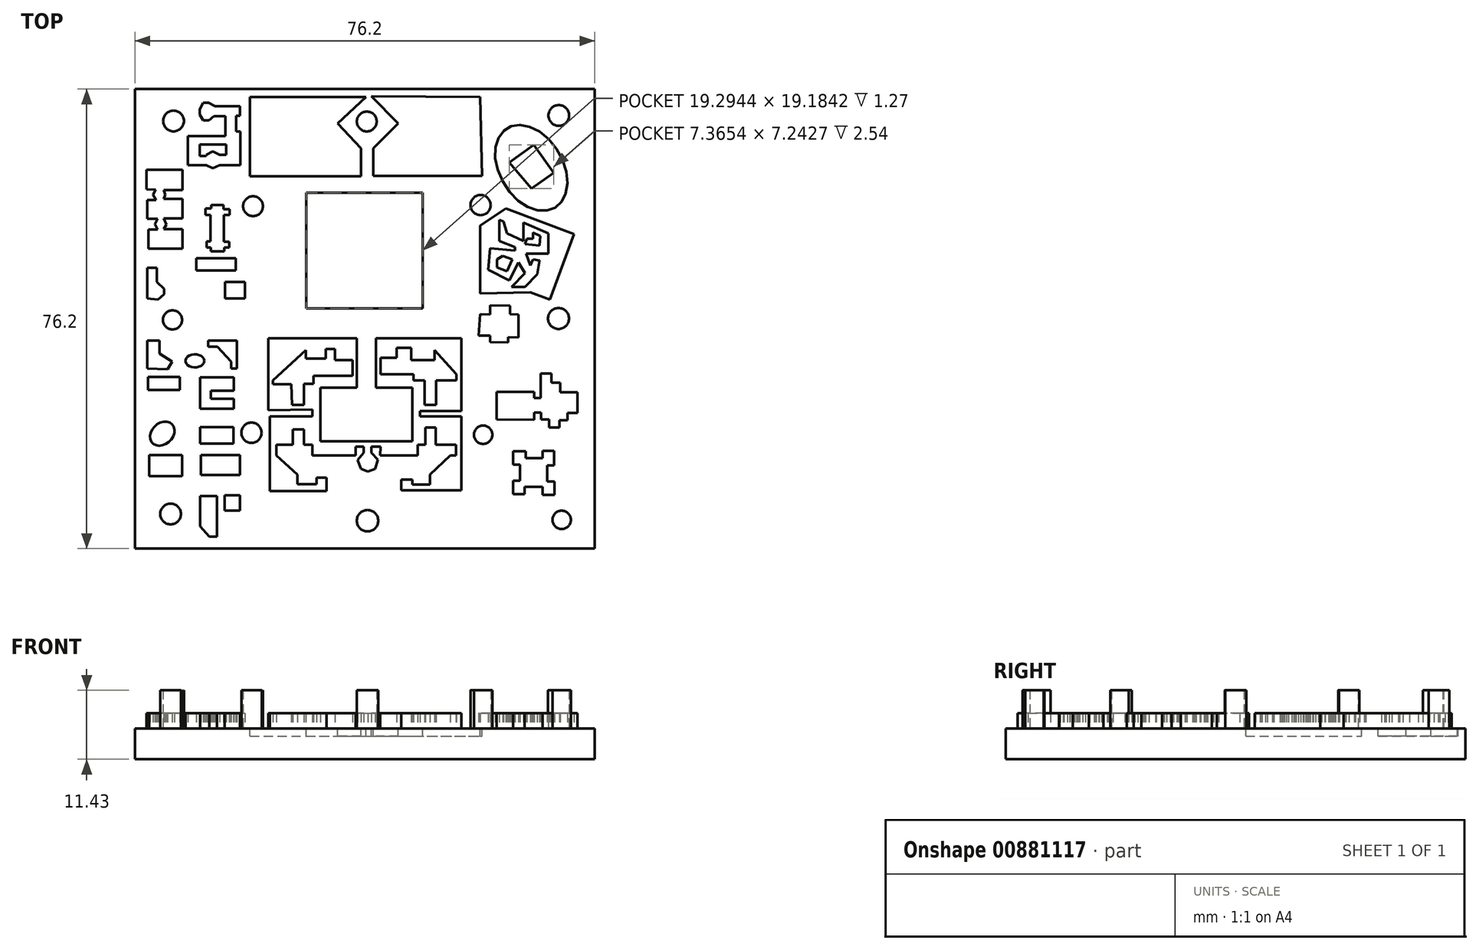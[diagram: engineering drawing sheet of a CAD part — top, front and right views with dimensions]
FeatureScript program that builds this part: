
annotation { "Feature Type Name" : "Feature", "Feature Type Description" : "" }
export const myFeature = defineFeature(function(context is Context, id is Id, definition is map)
    precondition{}
    {
        {
            var Q0;
            Q0=qCreatedBy(makeId("Top.planeOp"),FACE);
            var sketch = newSketch(context, id + "F0", { "sketchPlane" : qUnion([Q0])});
            skSolve(sketch);
        }
        {
            var Q0;
            Q0=qCreatedBy(makeId("Top.planeOp"),FACE);
            var sketch = newSketch(context, id + "F1", { "sketchPlane" : qUnion([Q0])});
            skLineSegment(sketch, "E0.bottom", {"start": v(-39.17, -36.08) * mm, "end": v(37.03, -36.08) * mm});
            skLineSegment(sketch, "E0.top", {"start": v(-39.17, 40.12) * mm, "end": v(37.03, 40.12) * mm});
            skLineSegment(sketch, "E0.left", {"start": v(-39.17, -36.08) * mm, "end": v(-39.17, 40.12) * mm});
            skLineSegment(sketch, "E0.right", {"start": v(37.03, -36.08) * mm, "end": v(37.03, 40.12) * mm});
            skSolve(sketch);
        }
        {
            var Q0;
            Q0 = qSketchRegion(id + "F1", true);
            extrude(context, id + "F2", {"entities" : qUnion([Q0]), "oppositeDirection" : true, "depth" : 5.08 * mm, "offsetDistance" : 25.4 * mm});
        }
        {
            var Q0;
            Q0=makeQuery(id+"F2.opExtrude","CAP_FACE",FACE,{"disambiguationData":[OSD([sQuery(id+"F1.wireOp",EDGE,"E0.bottom"),sQuery(id+"F1.wireOp",EDGE,"E0.top"),sQuery(id+"F1.wireOp",EDGE,"E0.left"),sQuery(id+"F1.wireOp",EDGE,"E0.right")])],"isStart":true});
            var sketch = newSketch(context, id + "F3", { "sketchPlane" : qUnion([Q0])});
            skCircle(sketch, "E1", {"center": v(-0.74, 34.74) * mm, "radius": 1.65 * mm});
            skCircle(sketch, "E2", {"center": v(-19.6, 20.7) * mm, "radius": 1.65 * mm});
            skCircle(sketch, "E3", {"center": v(-32.95, 1.84) * mm, "radius": 1.58 * mm});
            skCircle(sketch, "E4", {"center": v(-32.78, 34.83) * mm, "radius": 1.72 * mm});
            skCircle(sketch, "E5", {"center": v(18.13, 20.88) * mm, "radius": 1.67 * mm});
            skCircle(sketch, "E6", {"center": v(31.1, 35.74) * mm, "radius": 1.72 * mm});
            skCircle(sketch, "E7", {"center": v(31.04, 2.08) * mm, "radius": 1.74 * mm});
            skCircle(sketch, "E8", {"center": v(18.54, -17.2) * mm, "radius": 1.52 * mm});
            skCircle(sketch, "E9", {"center": v(-0.61, -31.45) * mm, "radius": 1.78 * mm});
            skCircle(sketch, "E10", {"center": v(-19.85, -16.87) * mm, "radius": 1.68 * mm});
            skCircle(sketch, "E11", {"center": v(-33.26, -30.34) * mm, "radius": 1.72 * mm});
            skCircle(sketch, "E12", {"center": v(31.56, -31.31) * mm, "radius": 1.52 * mm});
            skSolve(sketch);
        }
        {
            var Q0;
            Q0 = qSketchRegion(id + "F3", true);
            extrude(context, id + "F4", {"entities" : qUnion([Q0]), "operationType" : NewBodyOperationType.ADD, "depth" : 6.35 * mm, "offsetDistance" : 25.4 * mm});
        }
        {
            var Q0;
            Q0=makeQuery(id+"F2.opExtrude","CAP_FACE",FACE,{"disambiguationData":[OSD([sQuery(id+"F1.wireOp",EDGE,"E0.bottom"),sQuery(id+"F1.wireOp",EDGE,"E0.top"),sQuery(id+"F1.wireOp",EDGE,"E0.left"),sQuery(id+"F1.wireOp",EDGE,"E0.right")])],"isStart":true});
            var sketch = newSketch(context, id + "F5", { "sketchPlane" : qUnion([Q0])});
            skLineSegment(sketch, "E13.bottom", {"start": v(-10.75, 3.73) * mm, "end": v(8.55, 3.73) * mm});
            skLineSegment(sketch, "E13.top", {"start": v(-10.75, 22.91) * mm, "end": v(8.55, 22.91) * mm});
            skLineSegment(sketch, "E13.left", {"start": v(-10.75, 3.73) * mm, "end": v(-10.75, 22.91) * mm});
            skLineSegment(sketch, "E13.right", {"start": v(8.55, 3.73) * mm, "end": v(8.55, 22.91) * mm});
            skLineSegment(sketch, "E14", {"start": v(-20.12, 25.67) * mm, "end": v(-1.7, 25.67) * mm});
            skLineSegment(sketch, "E15", {"start": v(-1.7, 25.67) * mm, "end": v(-1.7, 30.3) * mm});
            skLineSegment(sketch, "E16", {"start": v(-1.7, 30.3) * mm, "end": v(-5.57, 34.4) * mm});
            skLineSegment(sketch, "E17", {"start": v(4.49, 34.4) * mm, "end": v(0.33, 30.3) * mm});
            skLineSegment(sketch, "E18", {"start": v(0.33, 30.3) * mm, "end": v(0.33, 25.7) * mm});
            skLineSegment(sketch, "E19", {"start": v(0.33, 25.7) * mm, "end": v(18.38, 25.7) * mm});
            skLineSegment(sketch, "E20", {"start": v(-20.12, 40.12) * mm, "end": v(-0.63, 40.12) * mm});
            skLineSegment(sketch, "E21", {"start": v(18.38, 40.12) * mm, "end": v(-0.63, 40.12) * mm});
            skLineSegment(sketch, "E22", {"start": v(-5.57, 34.4) * mm, "end": v(-0.88, 38.83) * mm});
            skLineSegment(sketch, "E23", {"start": v(4.49, 34.4) * mm, "end": v(0, 38.95) * mm});
            skLineSegment(sketch, "E24", {"start": v(-20.12, 25.67) * mm, "end": v(-20.12, 38.83) * mm});
            skLineSegment(sketch, "E25", {"start": v(18.04, 38.83) * mm, "end": v(18.38, 25.7) * mm});
            skLineSegment(sketch, "E26", {"start": v(-20.12, 38.83) * mm, "end": v(-0.88, 38.83) * mm});
            skLineSegment(sketch, "E27", {"start": v(0, 38.95) * mm, "end": v(18.04, 38.83) * mm});
            skSolve(sketch);
        }
        {
            var Q0;
            Q0 = qSketchRegion(id + "F5", true);
            extrude(context, id + "F6", {"entities" : qUnion([Q0]), "operationType" : NewBodyOperationType.REMOVE, "oppositeDirection" : true, "depth" : 1.27 * mm, "offsetDistance" : 25.4 * mm});
        }
        {
            var Q0;
            Q0=makeQuery(id+"F1.imprint","IMPRINT",FACE,{"disambiguationData":[TD([[makeQuery(id+"F1.imprint","IMPRINT",EDGE,{"derivedFrom":sQuery(id+"F1.wireOp",EDGE,"E0.bottom")}),1.0]])]});
            var sketch = newSketch(context, id + "F7", { "sketchPlane" : qUnion([Q0])});
            skLineSegment(sketch, "E28", {"start": v(-17.08, -13.15) * mm, "end": v(-17.08, -1.2) * mm});
            skLineSegment(sketch, "E29", {"start": v(-17.08, -1.2) * mm, "end": v(-2.39, -1.2) * mm});
            skLineSegment(sketch, "E30", {"start": v(-2.39, -1.2) * mm, "end": v(-2.39, -9.4) * mm});
            skLineSegment(sketch, "E31", {"start": v(-2.39, -9.4) * mm, "end": v(-8.41, -9.4) * mm});
            skLineSegment(sketch, "E32", {"start": v(-8.41, -9.4) * mm, "end": v(-8.41, -18.26) * mm});
            skLineSegment(sketch, "E33", {"start": v(-8.41, -18.26) * mm, "end": v(6.83, -18.26) * mm});
            skLineSegment(sketch, "E34", {"start": v(6.83, -18.26) * mm, "end": v(6.83, -9.4) * mm});
            skLineSegment(sketch, "E35", {"start": v(6.83, -9.4) * mm, "end": v(0.8, -9.4) * mm});
            skLineSegment(sketch, "E36", {"start": v(0.8, -9.4) * mm, "end": v(0.8, -1.2) * mm});
            skLineSegment(sketch, "E37", {"start": v(0.8, -1.2) * mm, "end": v(14.95, -1.2) * mm});
            skLineSegment(sketch, "E38", {"start": v(14.95, -1.2) * mm, "end": v(14.95, -13.24) * mm});
            skLineSegment(sketch, "E39", {"start": v(14.95, -13.24) * mm, "end": v(8.1, -13.24) * mm});
            skLineSegment(sketch, "E40", {"start": v(8.1, -13.24) * mm, "end": v(8.1, -14.15) * mm});
            skLineSegment(sketch, "E41", {"start": v(8.1, -14.15) * mm, "end": v(14.95, -14.15) * mm});
            skLineSegment(sketch, "E42", {"start": v(14.95, -14.15) * mm, "end": v(14.95, -26.38) * mm});
            skLineSegment(sketch, "E43", {"start": v(14.95, -26.38) * mm, "end": v(5, -26.38) * mm});
            skLineSegment(sketch, "E44", {"start": v(5, -26.38) * mm, "end": v(5, -24.65) * mm});
            skLineSegment(sketch, "E45", {"start": v(5, -24.65) * mm, "end": v(6.83, -24.65) * mm});
            skLineSegment(sketch, "E46", {"start": v(6.83, -24.65) * mm, "end": v(6.83, -25.47) * mm});
            skLineSegment(sketch, "E47", {"start": v(6.83, -25.47) * mm, "end": v(9.75, -25.47) * mm});
            skLineSegment(sketch, "E48", {"start": v(9.75, -25.47) * mm, "end": v(9.75, -23.83) * mm});
            skLineSegment(sketch, "E49", {"start": v(9.75, -23.83) * mm, "end": v(13.12, -20.63) * mm});
            skLineSegment(sketch, "E50", {"start": v(13.12, -20.63) * mm, "end": v(14.04, -20.63) * mm});
            skLineSegment(sketch, "E51", {"start": v(14.04, -20.63) * mm, "end": v(14.04, -18.85) * mm});
            skLineSegment(sketch, "E52", {"start": v(14.04, -18.85) * mm, "end": v(10.67, -18.85) * mm});
            skLineSegment(sketch, "E53", {"start": v(10.67, -18.85) * mm, "end": v(10.67, -15.97) * mm});
            skLineSegment(sketch, "E54", {"start": v(10.67, -15.97) * mm, "end": v(8.98, -15.97) * mm});
            skLineSegment(sketch, "E55", {"start": v(8.98, -15.97) * mm, "end": v(8.98, -18.85) * mm});
            skLineSegment(sketch, "E56", {"start": v(8.98, -18.85) * mm, "end": v(7.68, -18.85) * mm});
            skLineSegment(sketch, "E57", {"start": v(7.68, -18.85) * mm, "end": v(7.68, -20.63) * mm});
            skLineSegment(sketch, "E58", {"start": v(7.68, -20.63) * mm, "end": v(1.5, -20.63) * mm});
            skLineSegment(sketch, "E59", {"start": v(-1.7, -22.86) * mm, "end": v(-2.25, -21.4) * mm});
            skLineSegment(sketch, "E60", {"start": v(-9.79, -20.64) * mm, "end": v(-9.79, -18.85) * mm});
            skLineSegment(sketch, "E61", {"start": v(-9.79, -18.85) * mm, "end": v(-11.15, -18.85) * mm});
            skLineSegment(sketch, "E62", {"start": v(-11.15, -18.85) * mm, "end": v(-11.15, -16.3) * mm});
            skLineSegment(sketch, "E63", {"start": v(-11.15, -16.3) * mm, "end": v(-13, -16.3) * mm});
            skLineSegment(sketch, "E64", {"start": v(-13, -16.3) * mm, "end": v(-13, -18.85) * mm});
            skLineSegment(sketch, "E65", {"start": v(-13, -18.85) * mm, "end": v(-15.76, -18.85) * mm});
            skLineSegment(sketch, "E66", {"start": v(-15.76, -18.85) * mm, "end": v(-15.76, -20.64) * mm});
            skLineSegment(sketch, "E67", {"start": v(-15.76, -20.64) * mm, "end": v(-12.23, -23.84) * mm});
            skLineSegment(sketch, "E68", {"start": v(-12.23, -23.84) * mm, "end": v(-12.23, -25.41) * mm});
            skLineSegment(sketch, "E69", {"start": v(-12.23, -25.41) * mm, "end": v(-9.08, -25.41) * mm});
            skLineSegment(sketch, "E70", {"start": v(-9.08, -25.41) * mm, "end": v(-9.08, -24.33) * mm});
            skLineSegment(sketch, "E71", {"start": v(-9.08, -24.33) * mm, "end": v(-7.4, -24.33) * mm});
            skLineSegment(sketch, "E72", {"start": v(-7.4, -24.33) * mm, "end": v(-7.4, -26.55) * mm});
            skLineSegment(sketch, "E73", {"start": v(-7.4, -26.55) * mm, "end": v(-16.79, -26.55) * mm});
            skLineSegment(sketch, "E74", {"start": v(-16.79, -26.55) * mm, "end": v(-16.79, -14.18) * mm});
            skLineSegment(sketch, "E75", {"start": v(-16.79, -14.18) * mm, "end": v(-9.79, -14.18) * mm});
            skLineSegment(sketch, "E76", {"start": v(-9.79, -14.18) * mm, "end": v(-9.79, -13.04) * mm});
            skLineSegment(sketch, "E77", {"start": v(-9.79, -13.04) * mm, "end": v(-17.08, -13.15) * mm});
            skLineSegment(sketch, "E78", {"start": v(-13.15, -12.28) * mm, "end": v(-11.15, -12.28) * mm});
            skLineSegment(sketch, "E79", {"start": v(-11.15, -12.28) * mm, "end": v(-11.15, -8.75) * mm});
            skLineSegment(sketch, "E80", {"start": v(-11.15, -8.75) * mm, "end": v(-9.57, -8.75) * mm});
            skLineSegment(sketch, "E81", {"start": v(-9.57, -8.75) * mm, "end": v(-9.57, -7.4) * mm});
            skLineSegment(sketch, "E82", {"start": v(-9.57, -7.4) * mm, "end": v(-3.12, -7.4) * mm});
            skLineSegment(sketch, "E83", {"start": v(-3.12, -7.4) * mm, "end": v(-3.12, -4.8) * mm});
            skLineSegment(sketch, "E84", {"start": v(-3.12, -4.8) * mm, "end": v(-6.05, -4.8) * mm});
            skLineSegment(sketch, "E85", {"start": v(-6.05, -4.8) * mm, "end": v(-6.05, -2.95) * mm});
            skLineSegment(sketch, "E86", {"start": v(-6.05, -2.95) * mm, "end": v(-7.57, -2.95) * mm});
            skLineSegment(sketch, "E87", {"start": v(-7.57, -2.95) * mm, "end": v(-7.57, -4.58) * mm});
            skLineSegment(sketch, "E88", {"start": v(-7.57, -4.58) * mm, "end": v(-10.82, -4.58) * mm});
            skLineSegment(sketch, "E89", {"start": v(-10.82, -4.58) * mm, "end": v(-10.82, -3.16) * mm});
            skLineSegment(sketch, "E90", {"start": v(-10.82, -3.16) * mm, "end": v(-16.3, -8.21) * mm});
            skLineSegment(sketch, "E91", {"start": v(-16.3, -8.21) * mm, "end": v(-16.3, -8.8) * mm});
            skLineSegment(sketch, "E92", {"start": v(-16.3, -8.8) * mm, "end": v(-13.26, -8.8) * mm});
            skLineSegment(sketch, "E93", {"start": v(-13.26, -8.8) * mm, "end": v(-13.15, -12.28) * mm});
            skLineSegment(sketch, "E94", {"start": v(8.82, -8.21) * mm, "end": v(8.82, -12.28) * mm});
            skLineSegment(sketch, "E95", {"start": v(8.82, -12.28) * mm, "end": v(10.72, -12.28) * mm});
            skLineSegment(sketch, "E96", {"start": v(10.72, -12.28) * mm, "end": v(10.72, -8.21) * mm});
            skLineSegment(sketch, "E97", {"start": v(10.72, -8.21) * mm, "end": v(14.08, -8.21) * mm});
            skLineSegment(sketch, "E98", {"start": v(14.08, -8.21) * mm, "end": v(14.08, -7.18) * mm});
            skLineSegment(sketch, "E99", {"start": v(14.08, -7.18) * mm, "end": v(10.5, -3.16) * mm});
            skLineSegment(sketch, "E100", {"start": v(10.5, -3.16) * mm, "end": v(10.5, -4.85) * mm});
            skLineSegment(sketch, "E101", {"start": v(10.5, -4.85) * mm, "end": v(6.65, -4.85) * mm});
            skLineSegment(sketch, "E102", {"start": v(6.65, -4.85) * mm, "end": v(6.65, -2.78) * mm});
            skLineSegment(sketch, "E103", {"start": v(6.65, -2.78) * mm, "end": v(4.2, -2.78) * mm});
            skLineSegment(sketch, "E104", {"start": v(4.2, -2.78) * mm, "end": v(4.2, -4.47) * mm});
            skLineSegment(sketch, "E105", {"start": v(4.2, -4.47) * mm, "end": v(1.55, -4.47) * mm});
            skLineSegment(sketch, "E106", {"start": v(1.55, -4.47) * mm, "end": v(1.55, -7.18) * mm});
            skLineSegment(sketch, "E107", {"start": v(1.55, -7.18) * mm, "end": v(7.03, -7.18) * mm});
            skLineSegment(sketch, "E108", {"start": v(7.03, -7.18) * mm, "end": v(7.03, -8.21) * mm});
            skLineSegment(sketch, "E109", {"start": v(7.03, -8.21) * mm, "end": v(8.82, -8.21) * mm});
            skLineSegment(sketch, "E110", {"start": v(-9.79, -20.64) * mm, "end": v(-2.57, -20.64) * mm});
            skLineSegment(sketch, "E111", {"start": v(-2.57, -20.64) * mm, "end": v(-2.57, -19.2) * mm});
            skLineSegment(sketch, "E112", {"start": v(-2.57, -19.2) * mm, "end": v(-1.27, -19.2) * mm});
            skLineSegment(sketch, "E113", {"start": v(-1.27, -19.2) * mm, "end": v(-1.27, -20.2) * mm});
            skLineSegment(sketch, "E114", {"start": v(-1.27, -20.2) * mm, "end": v(-2.25, -21.4) * mm});
            skLineSegment(sketch, "E115", {"start": v(-1.7, -22.86) * mm, "end": v(-0.54, -23.3) * mm});
            skLineSegment(sketch, "E116", {"start": v(-0.54, -23.3) * mm, "end": v(0.65, -22.85) * mm});
            skLineSegment(sketch, "E117", {"start": v(0.65, -22.85) * mm, "end": v(1.07, -21.31) * mm});
            skLineSegment(sketch, "E118", {"start": v(1.07, -21.31) * mm, "end": v(0, -20.16) * mm});
            skLineSegment(sketch, "E119", {"start": v(0, -20.16) * mm, "end": v(0, -19.16) * mm});
            skLineSegment(sketch, "E120", {"start": v(0, -19.16) * mm, "end": v(1.53, -19.16) * mm});
            skLineSegment(sketch, "E121", {"start": v(1.53, -19.16) * mm, "end": v(1.5, -20.63) * mm});
            skSolve(sketch);
        }
        {
            var Q0;
            Q0 = qSketchRegion(id + "F7", true);
            extrude(context, id + "F8", {"entities" : qUnion([Q0]), "operationType" : NewBodyOperationType.ADD, "depth" : 2.54 * mm, "offsetDistance" : 25.4 * mm});
        }
        {
            var Q0;
            Q0=makeQuery(id+"F1.imprint","IMPRINT",FACE,{"disambiguationData":[TD([[makeQuery(id+"F1.imprint","IMPRINT",EDGE,{"derivedFrom":sQuery(id+"F1.wireOp",EDGE,"E0.bottom")}),1.0]])]});
            var sketch = newSketch(context, id + "F9", { "sketchPlane" : qUnion([Q0])});
            skLineSegment(sketch, "E122.bottom", {"start": v(-24.31, -29.8) * mm, "end": v(-21.75, -29.8) * mm});
            skLineSegment(sketch, "E122.top", {"start": v(-24.31, -27.25) * mm, "end": v(-21.75, -27.25) * mm});
            skLineSegment(sketch, "E122.left", {"start": v(-24.31, -29.8) * mm, "end": v(-24.31, -27.25) * mm});
            skLineSegment(sketch, "E122.right", {"start": v(-21.75, -29.8) * mm, "end": v(-21.75, -27.25) * mm});
            skLineSegment(sketch, "E123.bottom", {"start": v(-28.24, -23.87) * mm, "end": v(-21.75, -23.87) * mm});
            skLineSegment(sketch, "E123.top", {"start": v(-28.24, -20.58) * mm, "end": v(-21.75, -20.58) * mm});
            skLineSegment(sketch, "E123.left", {"start": v(-28.24, -23.87) * mm, "end": v(-28.24, -20.58) * mm});
            skLineSegment(sketch, "E123.right", {"start": v(-21.75, -23.87) * mm, "end": v(-21.75, -20.58) * mm});
            skLineSegment(sketch, "E124.bottom", {"start": v(-36.83, -24.05) * mm, "end": v(-31.35, -24.05) * mm});
            skLineSegment(sketch, "E124.top", {"start": v(-36.83, -20.58) * mm, "end": v(-31.35, -20.58) * mm});
            skLineSegment(sketch, "E124.left", {"start": v(-36.83, -24.05) * mm, "end": v(-36.83, -20.58) * mm});
            skLineSegment(sketch, "E124.right", {"start": v(-31.35, -24.05) * mm, "end": v(-31.35, -20.58) * mm});
            skLineSegment(sketch, "E125.bottom", {"start": v(-28.33, -18.66) * mm, "end": v(-22.85, -18.66) * mm});
            skLineSegment(sketch, "E125.top", {"start": v(-28.33, -15.92) * mm, "end": v(-22.85, -15.92) * mm});
            skLineSegment(sketch, "E125.left", {"start": v(-28.33, -18.66) * mm, "end": v(-28.33, -15.92) * mm});
            skLineSegment(sketch, "E125.right", {"start": v(-22.85, -18.66) * mm, "end": v(-22.85, -15.92) * mm});
            skLineSegment(sketch, "E126.bottom", {"start": v(-37.01, -9.8) * mm, "end": v(-31.71, -9.8) * mm});
            skLineSegment(sketch, "E126.top", {"start": v(-37.01, -7.6) * mm, "end": v(-31.71, -7.6) * mm});
            skLineSegment(sketch, "E126.left", {"start": v(-37.01, -9.8) * mm, "end": v(-37.01, -7.6) * mm});
            skLineSegment(sketch, "E126.right", {"start": v(-31.71, -9.8) * mm, "end": v(-31.71, -7.6) * mm});
            skLineSegment(sketch, "E127.bottom", {"start": v(-28.97, 10.04) * mm, "end": v(-22.48, 10.04) * mm});
            skLineSegment(sketch, "E127.top", {"start": v(-28.97, 12.05) * mm, "end": v(-22.48, 12.05) * mm});
            skLineSegment(sketch, "E127.left", {"start": v(-28.97, 10.04) * mm, "end": v(-28.97, 12.05) * mm});
            skLineSegment(sketch, "E127.right", {"start": v(-22.48, 10.04) * mm, "end": v(-22.48, 12.05) * mm});
            skLineSegment(sketch, "E128.bottom", {"start": v(-24.22, 5.38) * mm, "end": v(-20.93, 5.38) * mm});
            skLineSegment(sketch, "E128.top", {"start": v(-24.22, 8.12) * mm, "end": v(-20.93, 8.12) * mm});
            skLineSegment(sketch, "E128.left", {"start": v(-24.22, 5.38) * mm, "end": v(-24.22, 8.12) * mm});
            skLineSegment(sketch, "E128.right", {"start": v(-20.93, 5.38) * mm, "end": v(-20.93, 8.12) * mm});
            skLineSegment(sketch, "E129", {"start": v(-28.33, -32.37) * mm, "end": v(-28.33, -27.34) * mm});
            skLineSegment(sketch, "E130", {"start": v(-28.33, -27.34) * mm, "end": v(-25.6, -27.34) * mm});
            skLineSegment(sketch, "E131", {"start": v(-25.6, -27.34) * mm, "end": v(-25.6, -34.1) * mm});
            skLineSegment(sketch, "E132", {"start": v(-25.6, -34.1) * mm, "end": v(-26.87, -34.1) * mm});
            skLineSegment(sketch, "E133", {"start": v(-26.87, -34.1) * mm, "end": v(-28.33, -32.37) * mm});
            skLineSegment(sketch, "E134", {"start": v(-28.33, -7.7) * mm, "end": v(-28.33, -12.9) * mm});
            skLineSegment(sketch, "E135", {"start": v(-28.33, -12.9) * mm, "end": v(-22.76, -12.9) * mm});
            skLineSegment(sketch, "E136", {"start": v(-22.76, -12.9) * mm, "end": v(-22.76, -11.26) * mm});
            skLineSegment(sketch, "E137", {"start": v(-22.76, -11.26) * mm, "end": v(-26.6, -11.26) * mm});
            skLineSegment(sketch, "E138", {"start": v(-26.6, -11.26) * mm, "end": v(-26.6, -9.89) * mm});
            skLineSegment(sketch, "E139", {"start": v(-26.6, -9.89) * mm, "end": v(-22.76, -9.89) * mm});
            skLineSegment(sketch, "E140", {"start": v(-22.76, -9.89) * mm, "end": v(-22.76, -7.7) * mm});
            skLineSegment(sketch, "E141", {"start": v(-22.76, -7.7) * mm, "end": v(-28.33, -7.7) * mm});
            skLineSegment(sketch, "E142", {"start": v(-27.05, -1.57) * mm, "end": v(-22.3, -1.57) * mm});
            skLineSegment(sketch, "E143", {"start": v(-22.3, -1.57) * mm, "end": v(-22.3, -6.23) * mm});
            skLineSegment(sketch, "E144", {"start": v(-22.3, -6.23) * mm, "end": v(-23.22, -6.23) * mm});
            skLineSegment(sketch, "E145", {"start": v(-23.22, -6.23) * mm, "end": v(-23.22, -5.04) * mm});
            skLineSegment(sketch, "E146", {"start": v(-23.22, -5.04) * mm, "end": v(-25.5, -2.57) * mm});
            skLineSegment(sketch, "E147", {"start": v(-25.5, -2.57) * mm, "end": v(-27.05, -2.57) * mm});
            skLineSegment(sketch, "E148", {"start": v(-27.05, -2.57) * mm, "end": v(-27.05, -1.57) * mm});
            skLineSegment(sketch, "E149", {"start": v(-37.1, 5.38) * mm, "end": v(-37.1, 10.5) * mm});
            skLineSegment(sketch, "E150", {"start": v(-37.1, 10.5) * mm, "end": v(-35.55, 10.5) * mm});
            skLineSegment(sketch, "E151", {"start": v(-35.55, 10.5) * mm, "end": v(-35.55, 8.12) * mm});
            skLineSegment(sketch, "E152", {"start": v(-35.55, 8.12) * mm, "end": v(-34.36, 7.02) * mm});
            skLineSegment(sketch, "E153", {"start": v(-34.36, 7.02) * mm, "end": v(-34.36, 6.1) * mm});
            skLineSegment(sketch, "E154", {"start": v(-34.36, 6.1) * mm, "end": v(-35.37, 5.2) * mm});
            skLineSegment(sketch, "E155", {"start": v(-35.37, 5.2) * mm, "end": v(-37.1, 5.38) * mm});
            skLineSegment(sketch, "E156", {"start": v(-37.1, -6.23) * mm, "end": v(-37.1, -1.57) * mm});
            skLineSegment(sketch, "E157", {"start": v(-37.1, -1.57) * mm, "end": v(-35.1, -1.57) * mm});
            skLineSegment(sketch, "E158", {"start": v(-35.1, -1.57) * mm, "end": v(-35.1, -3.76) * mm});
            skLineSegment(sketch, "E159", {"start": v(-35.1, -3.76) * mm, "end": v(-33, -5.04) * mm});
            skLineSegment(sketch, "E160", {"start": v(-33, -5.04) * mm, "end": v(-33.77, -6.31) * mm});
            skLineSegment(sketch, "E161", {"start": v(-33.77, -6.31) * mm, "end": v(-37.1, -6.23) * mm});
            skEllipse(sketch, "E162", {"center": v(-29.25, -4.95) * mm, "majorRadius": 1.55 * mm, "minorRadius": 1.1 * mm, "majorAxis": v(1, 0)});
            skEllipse(sketch, "E163", {"center": v(-34.64, -17.01) * mm, "majorRadius": 2.26 * mm, "minorRadius": 1.75 * mm, "majorAxis": v(0.73, 0.69)});
            skLineSegment(sketch, "E164", {"start": v(-35.71, 23.43) * mm, "end": v(-36.15, 22.61) * mm});
            skLineSegment(sketch, "E165", {"start": v(-36.15, 22.61) * mm, "end": v(-35.66, 21.74) * mm});
            skLineSegment(sketch, "E166", {"start": v(-35.66, 21.74) * mm, "end": v(-37.13, 21.74) * mm});
            skLineSegment(sketch, "E167", {"start": v(-37.13, 21.74) * mm, "end": v(-37.13, 18.6) * mm});
            skLineSegment(sketch, "E168", {"start": v(-37.13, 18.6) * mm, "end": v(-35.39, 18.6) * mm});
            skLineSegment(sketch, "E169", {"start": v(-35.39, 18.6) * mm, "end": v(-35.88, 17.72) * mm});
            skLineSegment(sketch, "E170", {"start": v(-35.88, 17.72) * mm, "end": v(-35.39, 16.85) * mm});
            skLineSegment(sketch, "E171", {"start": v(-35.39, 16.85) * mm, "end": v(-36.96, 16.85) * mm});
            skLineSegment(sketch, "E172", {"start": v(-36.96, 16.85) * mm, "end": v(-36.96, 13.65) * mm});
            skLineSegment(sketch, "E173", {"start": v(-36.96, 13.65) * mm, "end": v(-31.31, 13.65) * mm});
            skLineSegment(sketch, "E174", {"start": v(-31.31, 13.65) * mm, "end": v(-31.31, 16.9) * mm});
            skLineSegment(sketch, "E175", {"start": v(-31.31, 16.9) * mm, "end": v(-34.4, 16.9) * mm});
            skLineSegment(sketch, "E176", {"start": v(-34.4, 16.9) * mm, "end": v(-33.97, 17.67) * mm});
            skLineSegment(sketch, "E177", {"start": v(-33.97, 17.67) * mm, "end": v(-34.4, 18.65) * mm});
            skLineSegment(sketch, "E178", {"start": v(-34.4, 18.65) * mm, "end": v(-31.31, 18.65) * mm});
            skLineSegment(sketch, "E179", {"start": v(-31.31, 18.65) * mm, "end": v(-31.31, 21.9) * mm});
            skLineSegment(sketch, "E180", {"start": v(-31.31, 21.9) * mm, "end": v(-34.4, 21.9) * mm});
            skLineSegment(sketch, "E181", {"start": v(-34.4, 21.9) * mm, "end": v(-34.11, 22.62) * mm});
            skLineSegment(sketch, "E182", {"start": v(-34.11, 22.62) * mm, "end": v(-34.4, 23.37) * mm});
            skLineSegment(sketch, "E183", {"start": v(-34.4, 23.37) * mm, "end": v(-31.3, 23.37) * mm});
            skLineSegment(sketch, "E184", {"start": v(-31.3, 23.37) * mm, "end": v(-31.3, 26.72) * mm});
            skLineSegment(sketch, "E185", {"start": v(-31.3, 26.72) * mm, "end": v(-37.23, 26.72) * mm});
            skLineSegment(sketch, "E186", {"start": v(-37.23, 26.72) * mm, "end": v(-37.23, 23.5) * mm});
            skLineSegment(sketch, "E187", {"start": v(-37.23, 23.5) * mm, "end": v(-35.71, 23.43) * mm});
            skLineSegment(sketch, "E188", {"start": v(-26.62, 19.23) * mm, "end": v(-26.62, 14.89) * mm});
            skLineSegment(sketch, "E189", {"start": v(-26.62, 14.89) * mm, "end": v(-27.3, 14.89) * mm});
            skLineSegment(sketch, "E190", {"start": v(-27.3, 14.89) * mm, "end": v(-27.3, 13.88) * mm});
            skLineSegment(sketch, "E191", {"start": v(-27.3, 13.88) * mm, "end": v(-26.6, 13.88) * mm});
            skLineSegment(sketch, "E192", {"start": v(-26.6, 13.88) * mm, "end": v(-26.6, 13.24) * mm});
            skLineSegment(sketch, "E193", {"start": v(-26.6, 13.24) * mm, "end": v(-24.39, 13.24) * mm});
            skLineSegment(sketch, "E194", {"start": v(-24.39, 13.24) * mm, "end": v(-24.39, 13.88) * mm});
            skLineSegment(sketch, "E195", {"start": v(-24.39, 13.88) * mm, "end": v(-23.54, 13.88) * mm});
            skLineSegment(sketch, "E196", {"start": v(-23.54, 13.88) * mm, "end": v(-23.54, 14.8) * mm});
            skLineSegment(sketch, "E197", {"start": v(-23.54, 14.8) * mm, "end": v(-24.4, 14.8) * mm});
            skLineSegment(sketch, "E198", {"start": v(-24.4, 14.8) * mm, "end": v(-24.4, 19.23) * mm});
            skLineSegment(sketch, "E199", {"start": v(-24.4, 19.23) * mm, "end": v(-23.5, 19.23) * mm});
            skLineSegment(sketch, "E200", {"start": v(-23.5, 19.23) * mm, "end": v(-23.5, 20.19) * mm});
            skLineSegment(sketch, "E201", {"start": v(-23.5, 20.19) * mm, "end": v(-24.48, 20.19) * mm});
            skLineSegment(sketch, "E202", {"start": v(-24.48, 20.19) * mm, "end": v(-24.48, 20.87) * mm});
            skLineSegment(sketch, "E203", {"start": v(-24.48, 20.87) * mm, "end": v(-26.53, 20.87) * mm});
            skLineSegment(sketch, "E204", {"start": v(-26.53, 20.87) * mm, "end": v(-26.53, 20.32) * mm});
            skLineSegment(sketch, "E205", {"start": v(-26.53, 20.32) * mm, "end": v(-27.5, 20.32) * mm});
            skLineSegment(sketch, "E206", {"start": v(-27.5, 20.32) * mm, "end": v(-27.5, 19.23) * mm});
            skLineSegment(sketch, "E207", {"start": v(-27.5, 19.23) * mm, "end": v(-26.62, 19.23) * mm});
            skLineSegment(sketch, "E208", {"start": v(-26.06, 35.62) * mm, "end": v(-24.16, 35.62) * mm});
            skLineSegment(sketch, "E209", {"start": v(-24.16, 35.62) * mm, "end": v(-24.16, 32.3) * mm});
            skLineSegment(sketch, "E210", {"start": v(-24.16, 32.3) * mm, "end": v(-30.38, 32.3) * mm});
            skLineSegment(sketch, "E211", {"start": v(-30.38, 32.3) * mm, "end": v(-30.38, 27.53) * mm});
            skLineSegment(sketch, "E212", {"start": v(-30.38, 27.53) * mm, "end": v(-27.33, 27.53) * mm});
            skLineSegment(sketch, "E213", {"start": v(-27.33, 27.53) * mm, "end": v(-26.24, 26.97) * mm});
            skLineSegment(sketch, "E214", {"start": v(-26.24, 26.97) * mm, "end": v(-25.1, 27.53) * mm});
            skLineSegment(sketch, "E215", {"start": v(-25.1, 27.53) * mm, "end": v(-21.72, 27.53) * mm});
            skLineSegment(sketch, "E216", {"start": v(-21.72, 27.53) * mm, "end": v(-21.72, 33.1) * mm});
            skLineSegment(sketch, "E217", {"start": v(-21.72, 33.1) * mm, "end": v(-22.43, 33.1) * mm});
            skLineSegment(sketch, "E218", {"start": v(-22.43, 33.1) * mm, "end": v(-22.43, 35.68) * mm});
            skLineSegment(sketch, "E219", {"start": v(-22.43, 35.68) * mm, "end": v(-21.75, 35.68) * mm});
            skLineSegment(sketch, "E220", {"start": v(-21.75, 35.68) * mm, "end": v(-21.75, 37.3) * mm});
            skLineSegment(sketch, "E221", {"start": v(-21.75, 37.3) * mm, "end": v(-25.89, 37.3) * mm});
            skLineSegment(sketch, "E222", {"start": v(-25.89, 37.3) * mm, "end": v(-26.94, 37.88) * mm});
            skLineSegment(sketch, "E223", {"start": v(-26.94, 37.88) * mm, "end": v(-27.88, 37.88) * mm});
            skLineSegment(sketch, "E224", {"start": v(-27.88, 37.88) * mm, "end": v(-28.41, 36.8) * mm});
            skLineSegment(sketch, "E225", {"start": v(-28.41, 36.8) * mm, "end": v(-28.41, 35.86) * mm});
            skLineSegment(sketch, "E226", {"start": v(-28.41, 35.86) * mm, "end": v(-27.85, 34.95) * mm});
            skLineSegment(sketch, "E227", {"start": v(-27.85, 34.95) * mm, "end": v(-26.91, 34.95) * mm});
            skLineSegment(sketch, "E228", {"start": v(-26.91, 34.95) * mm, "end": v(-26.06, 35.62) * mm});
            skLineSegment(sketch, "E229", {"start": v(-28.41, 29.02) * mm, "end": v(-28.41, 30.9) * mm});
            skLineSegment(sketch, "E230", {"start": v(-28.41, 30.9) * mm, "end": v(-24.04, 30.9) * mm});
            skLineSegment(sketch, "E231", {"start": v(-24.04, 30.9) * mm, "end": v(-24.04, 29.23) * mm});
            skLineSegment(sketch, "E232", {"start": v(-24.04, 29.23) * mm, "end": v(-25.13, 29.23) * mm});
            skLineSegment(sketch, "E233", {"start": v(-25.13, 29.23) * mm, "end": v(-26.24, 29.79) * mm});
            skLineSegment(sketch, "E234", {"start": v(-26.24, 29.79) * mm, "end": v(-27.33, 29.23) * mm});
            skLineSegment(sketch, "E235", {"start": v(-27.33, 29.23) * mm, "end": v(-27.33, 29.02) * mm});
            skLineSegment(sketch, "E236", {"start": v(-27.33, 29.02) * mm, "end": v(-28.41, 29.02) * mm});
            skLineSegment(sketch, "E237", {"start": v(23.5, -22.15) * mm, "end": v(23.5, -19.96) * mm});
            skLineSegment(sketch, "E238", {"start": v(23.5, -19.96) * mm, "end": v(25.6, -19.96) * mm});
            skLineSegment(sketch, "E239", {"start": v(25.6, -19.96) * mm, "end": v(25.6, -21.05) * mm});
            skLineSegment(sketch, "E240", {"start": v(25.6, -21.05) * mm, "end": v(28.42, -21.05) * mm});
            skLineSegment(sketch, "E241", {"start": v(28.42, -21.05) * mm, "end": v(28.42, -19.88) * mm});
            skLineSegment(sketch, "E242", {"start": v(28.42, -19.88) * mm, "end": v(30.3, -19.88) * mm});
            skLineSegment(sketch, "E243", {"start": v(30.3, -19.88) * mm, "end": v(30.3, -22.3) * mm});
            skLineSegment(sketch, "E244", {"start": v(30.3, -22.3) * mm, "end": v(29.18, -22.3) * mm});
            skLineSegment(sketch, "E245", {"start": v(29.18, -22.3) * mm, "end": v(29.18, -24.95) * mm});
            skLineSegment(sketch, "E246", {"start": v(29.18, -24.95) * mm, "end": v(30.36, -24.95) * mm});
            skLineSegment(sketch, "E247", {"start": v(30.36, -24.95) * mm, "end": v(30.36, -27.15) * mm});
            skLineSegment(sketch, "E248", {"start": v(30.36, -27.15) * mm, "end": v(28.42, -27.15) * mm});
            skLineSegment(sketch, "E249", {"start": v(28.42, -27.15) * mm, "end": v(28.42, -25.85) * mm});
            skLineSegment(sketch, "E250", {"start": v(28.42, -25.85) * mm, "end": v(25.45, -25.85) * mm});
            skLineSegment(sketch, "E251", {"start": v(25.45, -25.85) * mm, "end": v(25.45, -27.06) * mm});
            skLineSegment(sketch, "E252", {"start": v(25.45, -27.06) * mm, "end": v(23.52, -27.06) * mm});
            skLineSegment(sketch, "E253", {"start": v(23.52, -27.06) * mm, "end": v(23.52, -24.8) * mm});
            skLineSegment(sketch, "E254", {"start": v(23.52, -24.8) * mm, "end": v(24.67, -24.8) * mm});
            skLineSegment(sketch, "E255", {"start": v(24.67, -24.8) * mm, "end": v(24.67, -22.15) * mm});
            skLineSegment(sketch, "E256", {"start": v(24.67, -22.15) * mm, "end": v(23.5, -22.15) * mm});
            skLineSegment(sketch, "E257", {"start": v(20.8, -14.64) * mm, "end": v(20.8, -10.07) * mm});
            skLineSegment(sketch, "E258", {"start": v(20.8, -10.07) * mm, "end": v(27, -10.07) * mm});
            skLineSegment(sketch, "E259", {"start": v(27, -10.07) * mm, "end": v(27, -11.08) * mm});
            skLineSegment(sketch, "E260", {"start": v(27, -11.08) * mm, "end": v(28.06, -11.08) * mm});
            skLineSegment(sketch, "E261", {"start": v(28.06, -11.08) * mm, "end": v(28.06, -7.04) * mm});
            skLineSegment(sketch, "E262", {"start": v(28.06, -7.04) * mm, "end": v(29.86, -7.04) * mm});
            skLineSegment(sketch, "E263", {"start": v(29.86, -7.04) * mm, "end": v(29.86, -8.58) * mm});
            skLineSegment(sketch, "E264", {"start": v(29.86, -8.58) * mm, "end": v(31.35, -8.58) * mm});
            skLineSegment(sketch, "E265", {"start": v(31.35, -8.58) * mm, "end": v(31.35, -10.16) * mm});
            skLineSegment(sketch, "E266", {"start": v(31.35, -10.16) * mm, "end": v(34.2, -10.16) * mm});
            skLineSegment(sketch, "E267", {"start": v(34.2, -10.16) * mm, "end": v(34.2, -13.59) * mm});
            skLineSegment(sketch, "E268", {"start": v(34.2, -13.59) * mm, "end": v(32.54, -13.59) * mm});
            skLineSegment(sketch, "E269", {"start": v(32.54, -13.59) * mm, "end": v(32.54, -14.82) * mm});
            skLineSegment(sketch, "E270", {"start": v(32.54, -14.82) * mm, "end": v(31.22, -14.82) * mm});
            skLineSegment(sketch, "E271", {"start": v(31.22, -14.82) * mm, "end": v(31.22, -16) * mm});
            skLineSegment(sketch, "E272", {"start": v(31.22, -16) * mm, "end": v(29.46, -16) * mm});
            skLineSegment(sketch, "E273", {"start": v(29.46, -16) * mm, "end": v(29.46, -14.64) * mm});
            skLineSegment(sketch, "E274", {"start": v(29.46, -14.64) * mm, "end": v(28.14, -14.64) * mm});
            skLineSegment(sketch, "E275", {"start": v(28.14, -14.64) * mm, "end": v(28.14, -13.54) * mm});
            skLineSegment(sketch, "E276", {"start": v(28.14, -13.54) * mm, "end": v(27, -13.54) * mm});
            skLineSegment(sketch, "E277", {"start": v(27, -13.54) * mm, "end": v(27, -14.73) * mm});
            skLineSegment(sketch, "E278", {"start": v(27, -14.73) * mm, "end": v(20.8, -14.64) * mm});
            skLineSegment(sketch, "E279", {"start": v(18.05, 2.77) * mm, "end": v(19.72, 2.75) * mm});
            skLineSegment(sketch, "E280", {"start": v(19.72, 2.75) * mm, "end": v(19.72, 4.26) * mm});
            skLineSegment(sketch, "E281", {"start": v(19.72, 4.26) * mm, "end": v(22.98, 4.21) * mm});
            skLineSegment(sketch, "E282", {"start": v(22.98, 4.21) * mm, "end": v(22.98, 2.77) * mm});
            skLineSegment(sketch, "E283", {"start": v(22.98, 2.77) * mm, "end": v(24.38, 2.75) * mm});
            skLineSegment(sketch, "E284", {"start": v(24.38, 2.75) * mm, "end": v(24.38, -1.05) * mm});
            skLineSegment(sketch, "E285", {"start": v(24.38, -1.05) * mm, "end": v(22.7, -1.02) * mm});
            skLineSegment(sketch, "E286", {"start": v(22.7, -1.02) * mm, "end": v(22.7, -1.89) * mm});
            skLineSegment(sketch, "E287", {"start": v(22.7, -1.89) * mm, "end": v(19.72, -1.84) * mm});
            skLineSegment(sketch, "E288", {"start": v(19.72, -1.84) * mm, "end": v(19.72, -0.77) * mm});
            skLineSegment(sketch, "E289", {"start": v(19.72, -0.77) * mm, "end": v(17.77, -0.77) * mm});
            skLineSegment(sketch, "E290", {"start": v(17.77, -0.77) * mm, "end": v(18.05, 2.77) * mm});
            skLineSegment(sketch, "E291", {"start": v(26.4, 6.4) * mm, "end": v(29.58, 5.22) * mm});
            skLineSegment(sketch, "E292", {"start": v(29.58, 5.22) * mm, "end": v(33.62, 16.08) * mm});
            skLineSegment(sketch, "E293", {"start": v(33.62, 16.08) * mm, "end": v(22.3, 20.3) * mm});
            skLineSegment(sketch, "E294", {"start": v(22.3, 20.3) * mm, "end": v(18.05, 17.49) * mm});
            skLineSegment(sketch, "E295", {"start": v(18.05, 17.49) * mm, "end": v(18.05, 6.25) * mm});
            skLineSegment(sketch, "E296", {"start": v(18.05, 6.25) * mm, "end": v(26.4, 6.4) * mm});
            skLineSegment(sketch, "E297", {"start": v(22.5, 16.17) * mm, "end": v(25.26, 14.92) * mm});
            skLineSegment(sketch, "E298", {"start": v(25.26, 14.92) * mm, "end": v(25.26, 17.95) * mm});
            skLineSegment(sketch, "E299", {"start": v(25.26, 17.95) * mm, "end": v(29.34, 16.17) * mm});
            skLineSegment(sketch, "E300", {"start": v(29.34, 16.17) * mm, "end": v(29.34, 12.81) * mm});
            skLineSegment(sketch, "E301", {"start": v(29.34, 12.81) * mm, "end": v(25.65, 12.81) * mm});
            skLineSegment(sketch, "E302", {"start": v(25.65, 12.81) * mm, "end": v(26.4, 10.84) * mm});
            skLineSegment(sketch, "E303", {"start": v(25.46, 7.28) * mm, "end": v(23.28, 7.28) * mm});
            skLineSegment(sketch, "E304", {"start": v(23.28, 7.28) * mm, "end": v(25.46, 9.59) * mm});
            skLineSegment(sketch, "E305", {"start": v(25.46, 9.59) * mm, "end": v(24.4, 11.37) * mm});
            skLineSegment(sketch, "E306", {"start": v(24.4, 11.37) * mm, "end": v(22.89, 8.4) * mm});
            skLineSegment(sketch, "E307", {"start": v(22.89, 8.4) * mm, "end": v(19.4, 10.18) * mm});
            skLineSegment(sketch, "E308", {"start": v(19.4, 10.18) * mm, "end": v(19.72, 13.74) * mm});
            skLineSegment(sketch, "E309", {"start": v(19.72, 13.74) * mm, "end": v(23.84, 13.36) * mm});
            skLineSegment(sketch, "E310", {"start": v(23.84, 13.36) * mm, "end": v(23.84, 13.93) * mm});
            skLineSegment(sketch, "E311", {"start": v(23.84, 13.93) * mm, "end": v(21.24, 14.92) * mm});
            skLineSegment(sketch, "E312", {"start": v(26.57, 23.61) * mm, "end": v(30.26, 26.25) * mm});
            skLineSegment(sketch, "E313", {"start": v(30.26, 26.25) * mm, "end": v(26.97, 30.85) * mm});
            skLineSegment(sketch, "E314", {"start": v(26.97, 30.85) * mm, "end": v(22.9, 27.95) * mm});
            skLineSegment(sketch, "E315", {"start": v(22.9, 27.95) * mm, "end": v(26.57, 23.61) * mm});
            skEllipse(sketch, "E316", {"center": v(26.52, 27.06) * mm, "majorRadius": 7.7 * mm, "minorRadius": 5.23 * mm, "majorAxis": v(0.52, -0.86)});
            skLineSegment(sketch, "E317", {"start": v(21.24, 14.92) * mm, "end": v(21.24, 18.41) * mm});
            skLineSegment(sketch, "E318", {"start": v(21.24, 18.41) * mm, "end": v(21.9, 18.16) * mm});
            skLineSegment(sketch, "E319", {"start": v(21.9, 18.16) * mm, "end": v(22.5, 16.17) * mm});
            skLineSegment(sketch, "E320", {"start": v(25.46, 7.28) * mm, "end": v(27.53, 9.41) * mm});
            skLineSegment(sketch, "E321", {"start": v(27.53, 9.41) * mm, "end": v(27.87, 11.7) * mm});
            skLineSegment(sketch, "E322", {"start": v(27.87, 11.7) * mm, "end": v(26.81, 11.85) * mm});
            skLineSegment(sketch, "E323", {"start": v(26.81, 11.85) * mm, "end": v(26.4, 10.84) * mm});
            skLineSegment(sketch, "E324", {"start": v(22.5, 9.88) * mm, "end": v(20.81, 10.52) * mm});
            skLineSegment(sketch, "E325", {"start": v(20.81, 10.52) * mm, "end": v(20.81, 11.87) * mm});
            skLineSegment(sketch, "E326", {"start": v(20.81, 11.87) * mm, "end": v(21.8, 12.47) * mm});
            skLineSegment(sketch, "E327", {"start": v(21.8, 12.47) * mm, "end": v(23.38, 11.87) * mm});
            skLineSegment(sketch, "E328", {"start": v(23.38, 11.87) * mm, "end": v(22.5, 9.88) * mm});
            skLineSegment(sketch, "E329", {"start": v(25.46, 14.4) * mm, "end": v(25.8, 15.33) * mm});
            skLineSegment(sketch, "E330", {"start": v(25.8, 15.33) * mm, "end": v(26.8, 15.33) * mm});
            skLineSegment(sketch, "E331", {"start": v(26.8, 15.33) * mm, "end": v(26.84, 16.34) * mm});
            skLineSegment(sketch, "E332", {"start": v(26.84, 16.34) * mm, "end": v(28.05, 15.74) * mm});
            skLineSegment(sketch, "E333", {"start": v(28.05, 15.74) * mm, "end": v(27.87, 14.2) * mm});
            skLineSegment(sketch, "E334", {"start": v(27.87, 14.2) * mm, "end": v(25.46, 14.4) * mm});
            skSolve(sketch);
        }
        {
            var Q0;
            Q0 = qSketchRegion(id + "F9", true);
            extrude(context, id + "F10", {"entities" : qUnion([Q0]), "operationType" : NewBodyOperationType.ADD, "depth" : 2.54 * mm, "offsetDistance" : 25.4 * mm});
        }
        {
            var Q0;
            Q0=makeQuery(id+"F9.imprint","IMPRINT",FACE,{"disambiguationData":[TD([[makeQuery(id+"F9.imprint","IMPRINT",EDGE,{"derivedFrom":sQuery(id+"F9.wireOp",EDGE,"E324")}),-1.0]])]});
            var Q1;
            Q1=makeQuery(id+"F9.imprint","IMPRINT",FACE,{"disambiguationData":[TD([[makeQuery(id+"F9.imprint","IMPRINT",EDGE,{"derivedFrom":sQuery(id+"F9.wireOp",EDGE,"E329")}),-1.0]])]});
            extrude(context, id + "F11", {"entities" : qUnion([Q0, Q1]), "operationType" : NewBodyOperationType.ADD, "depth" : 2.54 * mm, "offsetDistance" : 25.4 * mm});
        }
    });
